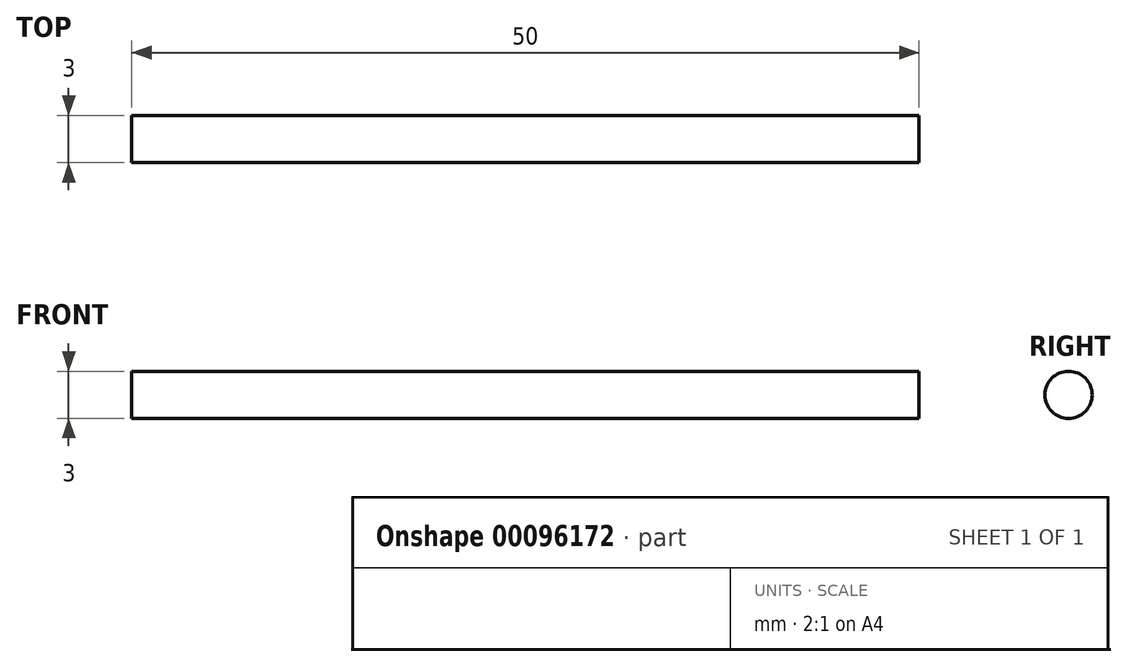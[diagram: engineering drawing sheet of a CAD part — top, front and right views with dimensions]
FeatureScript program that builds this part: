
annotation { "Feature Type Name" : "Feature", "Feature Type Description" : "" }
export const myFeature = defineFeature(function(context is Context, id is Id, definition is map)
    precondition{}
    {
        {
            var Q0;
            Q0=qCreatedBy(makeId("Right.planeOp"),FACE);
            var sketch = newSketch(context, id + "F0", { "sketchPlane" : qUnion([Q0])});
            skCircle(sketch, "E0", {"center": v(0, 0) * mm, "radius": 1.5 * mm});
            skSolve(sketch);
        }
        {
            var Q0;
            Q0=qSketchRegion(id+"F0",true);
            extrude(context, id + "F1", {"entities" : qUnion([Q0]), "depth" : 25 * mm, "hasSecondDirection" : true, "secondDirectionOppositeDirection" : true, "secondDirectionDepth" : 25 * mm});
        }
    });
